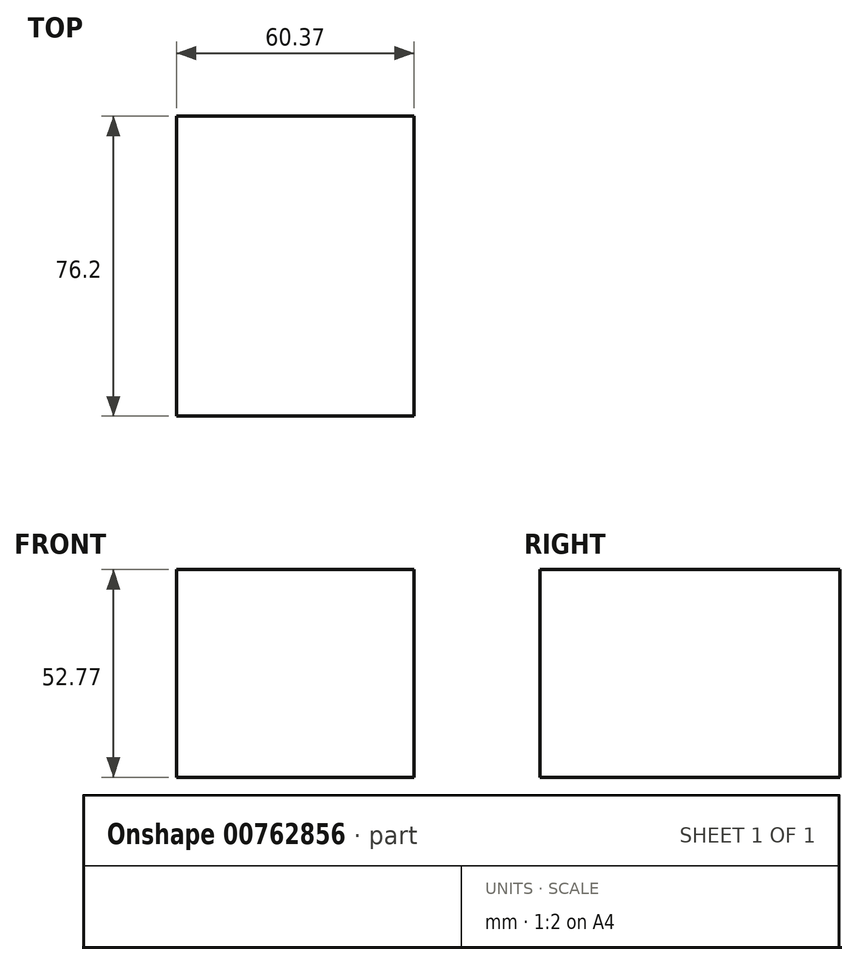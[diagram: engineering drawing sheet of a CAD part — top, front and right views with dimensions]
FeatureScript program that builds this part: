
annotation { "Feature Type Name" : "Feature", "Feature Type Description" : "" }
export const myFeature = defineFeature(function(context is Context, id is Id, definition is map)
    precondition{}
    {
        {
            var Q0;
            Q0=qCreatedBy(makeId("Front.planeOp"),FACE);
            var sketch = newSketch(context, id + "F0", { "sketchPlane" : qUnion([Q0])});
            skLineSegment(sketch, "E0.bottom", {"start": v(-32.73, 17.51) * mm, "end": v(27.64, 17.51) * mm});
            skLineSegment(sketch, "E0.top", {"start": v(-32.73, -35.26) * mm, "end": v(27.64, -35.26) * mm});
            skLineSegment(sketch, "E0.left", {"start": v(-32.73, 17.51) * mm, "end": v(-32.73, -35.26) * mm});
            skLineSegment(sketch, "E0.right", {"start": v(27.64, 17.51) * mm, "end": v(27.64, -35.26) * mm});
            skSolve(sketch);
        }
        {
            var Q0;
            Q0 = qSketchRegion(id + "F0", true);
            extrude(context, id + "F1", {"entities" : qUnion([Q0]), "depth" : 76.2 * mm, "offsetDistance" : 25.4 * mm});
        }
    });
